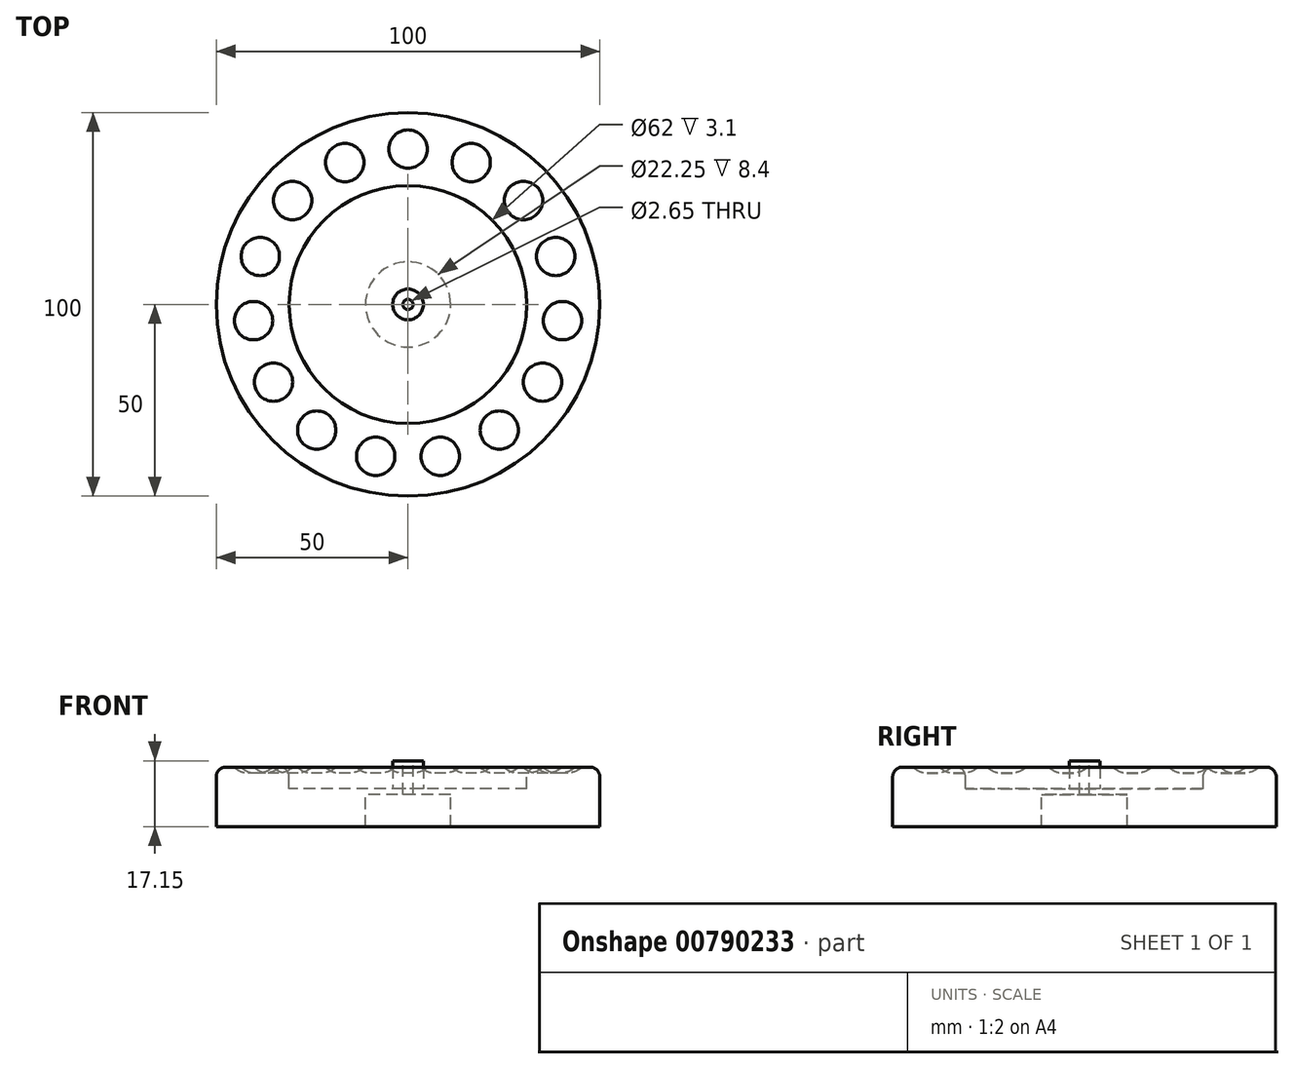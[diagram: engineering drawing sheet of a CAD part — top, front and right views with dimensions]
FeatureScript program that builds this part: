
annotation { "Feature Type Name" : "Feature", "Feature Type Description" : "" }
export const myFeature = defineFeature(function(context is Context, id is Id, definition is map)
    precondition{}
    {
        {
            var Q0;
            Q0=qCreatedBy(makeId("Top.planeOp"),FACE);
            var sketch = newSketch(context, id + "F0", { "sketchPlane" : qUnion([Q0])});
            skCircle(sketch, "E0", {"center": v(0, 0) * mm, "radius": 50 * mm});
            skSolve(sketch);
        }
        {
            var Q0;
            Q0 = qSketchRegion(id + "F0", true);
            extrude(context, id + "F1", {"entities" : qUnion([Q0]), "depth" : 15.5 * mm, "offsetDistance" : 25 * mm});
        }
        {
            var Q0;
            Q0=makeQuery(id+"F1.opExtrude","CAP_FACE",FACE,{"disambiguationData":[OSD([sQuery(id+"F0.wireOp",EDGE,"E0")])],"isStart":false});
            var sketch = newSketch(context, id + "F2", { "sketchPlane" : qUnion([Q0])});
            skCircle(sketch, "E1", {"center": v(0, 0) * mm, "radius": 31 * mm});
            skSolve(sketch);
        }
        {
            var Q0;
            Q0 = qSketchRegion(id + "F2", true);
            extrude(context, id + "F3", {"entities" : qUnion([Q0]), "operationType" : NewBodyOperationType.REMOVE, "oppositeDirection" : true, "depth" : 7.1 * mm, "offsetDistance" : 25 * mm});
        }
        {
            var Q0;
            Q0=makeQuery(id+"F3.boolean.opBoolean","COPY",FACE,{"derivedFrom":makeQuery(id+"F3.opExtrude","CAP_FACE",FACE,{"disambiguationData":[OSD([sQuery(id+"F2.wireOp",EDGE,"E1")])],"isStart":false})});
            var sketch = newSketch(context, id + "F4", { "sketchPlane" : qUnion([Q0])});
            skCircle(sketch, "E2", {"center": v(0, 0) * mm, "radius": 11.12 * mm});
            skSolve(sketch);
        }
        {
            var Q0;
            Q0 = qSketchRegion(id + "F4", true);
            extrude(context, id + "F5", {"entities" : qUnion([Q0]), "operationType" : NewBodyOperationType.REMOVE, "oppositeDirection" : true, "depth" : 9 * mm, "offsetDistance" : 25 * mm});
        }
        {
            var Q0;
            Q0=makeQuery(id+"F1.opExtrude","CAP_FACE",FACE,{"disambiguationData":[OSD([sQuery(id+"F0.wireOp",EDGE,"E0")])],"isStart":false});
            fillet(context, id + "F6", {"entities" : qUnion([Q0]), "radius" : 2.5 * mm, "tangentPropagation" : true, "allowEdgeOverflow" : false});
        }
        {
            var Q0;
            Q0=makeQuery(id+"F1.opExtrude","CAP_FACE",FACE,{"disambiguationData":[OSD([sQuery(id+"F0.wireOp",EDGE,"E0")])],"isStart":false});
            var sketch = newSketch(context, id + "F7", { "sketchPlane" : qUnion([Q0])});
            skCircle(sketch, "E3", {"center": v(0, 40.5) * mm, "radius": 5 * mm});
            skCircle(sketch, "E4.1.0", {"center": v(-16.47, 37) * mm, "radius": 5 * mm});
            skCircle(sketch, "E4.2.0", {"center": v(-30.1, 27.1) * mm, "radius": 5 * mm});
            skCircle(sketch, "E4.3.0", {"center": v(-38.52, 12.52) * mm, "radius": 5 * mm});
            skCircle(sketch, "E4.4.0", {"center": v(-40.28, -4.23) * mm, "radius": 5 * mm});
            skCircle(sketch, "E4.5.0", {"center": v(-35.07, -20.25) * mm, "radius": 5 * mm});
            skCircle(sketch, "E4.6.0", {"center": v(-23.8, -32.77) * mm, "radius": 5 * mm});
            skCircle(sketch, "E4.7.0", {"center": v(-8.42, -39.61) * mm, "radius": 5 * mm});
            skCircle(sketch, "E4.8.0", {"center": v(8.42, -39.61) * mm, "radius": 5 * mm});
            skCircle(sketch, "E4.9.0", {"center": v(23.8, -32.77) * mm, "radius": 5 * mm});
            skCircle(sketch, "E4.10.0", {"center": v(35.07, -20.25) * mm, "radius": 5 * mm});
            skCircle(sketch, "E4.11.0", {"center": v(40.28, -4.23) * mm, "radius": 5 * mm});
            skCircle(sketch, "E4.12.0", {"center": v(38.52, 12.52) * mm, "radius": 5 * mm});
            skCircle(sketch, "E4.13.0", {"center": v(30.1, 27.1) * mm, "radius": 5 * mm});
            skCircle(sketch, "E4.14.0", {"center": v(16.47, 37) * mm, "radius": 5 * mm});
            skPoint(sketch, "E4.center", {"position": v(0, 0) * mm});
            skSolve(sketch);
        }
        {
            var Q0;
            Q0 = qSketchRegion(id + "F7", true);
            extrude(context, id + "F8", {"entities" : qUnion([Q0]), "operationType" : NewBodyOperationType.REMOVE, "oppositeDirection" : true, "depth" : 1.5 * mm, "offsetDistance" : 25 * mm});
        }
        {
            var Q0;
            Q0=makeQuery(id+"F8.boolean.opBoolean","COPY",FACE,{"derivedFrom":makeQuery(id+"F8.opExtrude","CAP_FACE",FACE,{"disambiguationData":[OSD([sQuery(id+"F7.wireOp",EDGE,"E3")])],"isStart":false})});
            var Q1;
            Q1=makeQuery(id+"F8.boolean.opBoolean","COPY",FACE,{"derivedFrom":makeQuery(id+"F8.opExtrude","CAP_FACE",FACE,{"disambiguationData":[OSD([sQuery(id+"F7.wireOp",EDGE,"E4.1.0")])],"isStart":false})});
            var Q2;
            Q2=makeQuery(id+"F8.boolean.opBoolean","COPY",FACE,{"derivedFrom":makeQuery(id+"F8.opExtrude","CAP_FACE",FACE,{"disambiguationData":[OSD([sQuery(id+"F7.wireOp",EDGE,"E4.2.0")])],"isStart":false})});
            var Q3;
            Q3=makeQuery(id+"F8.boolean.opBoolean","COPY",FACE,{"derivedFrom":makeQuery(id+"F8.opExtrude","CAP_FACE",FACE,{"disambiguationData":[OSD([sQuery(id+"F7.wireOp",EDGE,"E4.3.0")])],"isStart":false})});
            var Q4;
            Q4=makeQuery(id+"F8.boolean.opBoolean","COPY",FACE,{"derivedFrom":makeQuery(id+"F8.opExtrude","CAP_FACE",FACE,{"disambiguationData":[OSD([sQuery(id+"F7.wireOp",EDGE,"E4.4.0")])],"isStart":false})});
            var Q5;
            Q5=makeQuery(id+"F8.boolean.opBoolean","COPY",FACE,{"derivedFrom":makeQuery(id+"F8.opExtrude","CAP_FACE",FACE,{"disambiguationData":[OSD([sQuery(id+"F7.wireOp",EDGE,"E4.5.0")])],"isStart":false})});
            var Q6;
            Q6=makeQuery(id+"F8.boolean.opBoolean","COPY",FACE,{"derivedFrom":makeQuery(id+"F8.opExtrude","CAP_FACE",FACE,{"disambiguationData":[OSD([sQuery(id+"F7.wireOp",EDGE,"E4.6.0")])],"isStart":false})});
            var Q7;
            Q7=makeQuery(id+"F8.boolean.opBoolean","COPY",FACE,{"derivedFrom":makeQuery(id+"F8.opExtrude","CAP_FACE",FACE,{"disambiguationData":[OSD([sQuery(id+"F7.wireOp",EDGE,"E4.7.0")])],"isStart":false})});
            var Q8;
            Q8=makeQuery(id+"F8.boolean.opBoolean","COPY",FACE,{"derivedFrom":makeQuery(id+"F8.opExtrude","CAP_FACE",FACE,{"disambiguationData":[OSD([sQuery(id+"F7.wireOp",EDGE,"E4.8.0")])],"isStart":false})});
            var Q9;
            Q9=makeQuery(id+"F8.boolean.opBoolean","COPY",FACE,{"derivedFrom":makeQuery(id+"F8.opExtrude","CAP_FACE",FACE,{"disambiguationData":[OSD([sQuery(id+"F7.wireOp",EDGE,"E4.9.0")])],"isStart":false})});
            var Q10;
            Q10=makeQuery(id+"F8.boolean.opBoolean","COPY",FACE,{"derivedFrom":makeQuery(id+"F8.opExtrude","CAP_FACE",FACE,{"disambiguationData":[OSD([sQuery(id+"F7.wireOp",EDGE,"E4.10.0")])],"isStart":false})});
            var Q11;
            Q11=makeQuery(id+"F8.boolean.opBoolean","COPY",FACE,{"derivedFrom":makeQuery(id+"F8.opExtrude","CAP_FACE",FACE,{"disambiguationData":[OSD([sQuery(id+"F7.wireOp",EDGE,"E4.11.0")])],"isStart":false})});
            var Q12;
            Q12=makeQuery(id+"F8.boolean.opBoolean","COPY",FACE,{"derivedFrom":makeQuery(id+"F8.opExtrude","CAP_FACE",FACE,{"disambiguationData":[OSD([sQuery(id+"F7.wireOp",EDGE,"E4.12.0")])],"isStart":false})});
            var Q13;
            Q13=makeQuery(id+"F8.boolean.opBoolean","COPY",FACE,{"derivedFrom":makeQuery(id+"F8.opExtrude","CAP_FACE",FACE,{"disambiguationData":[OSD([sQuery(id+"F7.wireOp",EDGE,"E4.13.0")])],"isStart":false})});
            var Q14;
            Q14=makeQuery(id+"F8.boolean.opBoolean","COPY",FACE,{"derivedFrom":makeQuery(id+"F8.opExtrude","CAP_FACE",FACE,{"disambiguationData":[OSD([sQuery(id+"F7.wireOp",EDGE,"E4.14.0")])],"isStart":false})});
            fillet(context, id + "F9", {"entities" : qUnion([Q0, Q1, Q2, Q3, Q4, Q5, Q6, Q7, Q8, Q9, Q10, Q11, Q12, Q13, Q14]), "radius" : 5 * mm, "tangentPropagation" : true, "allowEdgeOverflow" : false});
        }
        {
            var Q0;
            Q0=makeQuery(id+"F3.boolean.opBoolean","COPY",FACE,{"derivedFrom":makeQuery(id+"F3.opExtrude","CAP_FACE",FACE,{"disambiguationData":[OSD([sQuery(id+"F2.wireOp",EDGE,"E1")])],"isStart":false})});
            var sketch = newSketch(context, id + "F10", { "sketchPlane" : qUnion([Q0])});
            skCircle(sketch, "E5", {"center": v(0, 0) * mm, "radius": 31.06 * mm});
            skSolve(sketch);
        }
        {
            var Q0;
            Q0 = qSketchRegion(id + "F10", true);
            extrude(context, id + "F11", {"entities" : qUnion([Q0]), "operationType" : NewBodyOperationType.ADD, "depth" : 1.5 * mm, "offsetDistance" : 25 * mm});
        }
        {
            var Q0;
            Q0=makeQuery(id+"F11.opExtrude","CAP_FACE",FACE,{"disambiguationData":[OSD([sQuery(id+"F10.wireOp",EDGE,"E5")])],"isStart":false});
            var sketch = newSketch(context, id + "F12", { "sketchPlane" : qUnion([Q0])});
            skCircle(sketch, "E6", {"center": v(0, 0) * mm, "radius": 4 * mm});
            skSolve(sketch);
        }
        {
            var Q0;
            Q0 = qSketchRegion(id + "F12", true);
            extrude(context, id + "F13", {"entities" : qUnion([Q0]), "operationType" : NewBodyOperationType.ADD, "depth" : 7.25 * mm, "offsetDistance" : 25 * mm});
        }
        {
            var Q0;
            Q0=makeQuery(id+"F13.opExtrude","CAP_FACE",FACE,{"disambiguationData":[OSD([sQuery(id+"F12.wireOp",EDGE,"E6")])],"isStart":false});
            var sketch = newSketch(context, id + "F14", { "sketchPlane" : qUnion([Q0])});
            skPoint(sketch, "E7", {"position": v(0, 0) * mm});
            skSolve(sketch);
        }
        {
            var Q0;
            Q0=sQuery(id+"F14.wireOp",VERTEX,"E7");
            var Q1;
            Q1=makeQuery(id+"F1.opExtrude","SWEPT_BODY",BODY,{"disambiguationData":[OSD([sQuery(id+"F0.wireOp",EDGE,"E0")])]});
            hole(context, id + "F15", {"style" : HoleStyle.SIMPLE, "endStyle" : HoleEndStyle.BLIND, "holeDiameter" : 2.65 * mm, "majorDiameter" : 5 * mm, "holeDepth" : 10 * mm, "isTappedThrough" : true, "tappedDepth" : 12 * mm, "tapClearance" : 3, "startFromSketch" : true, "locations" : qUnion([Q0]), "scope" : qUnion([Q1])});
        }
    });
